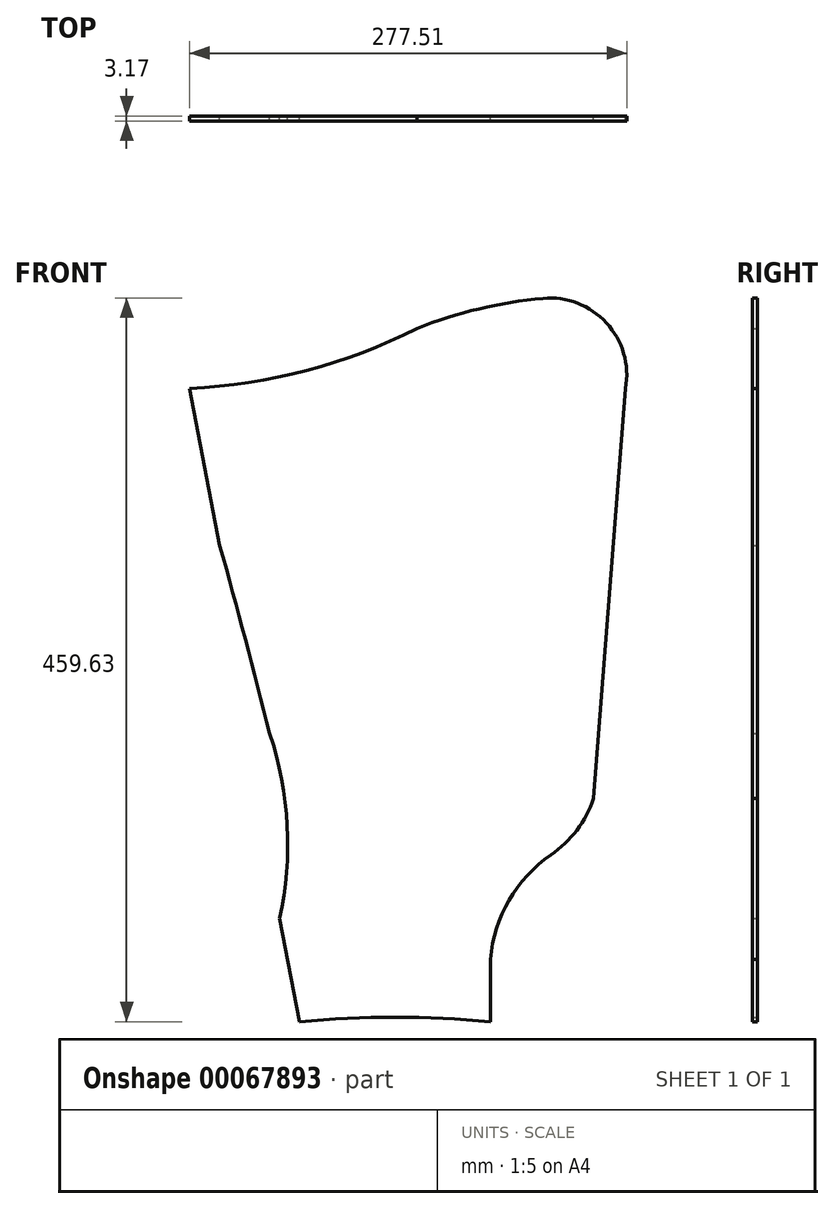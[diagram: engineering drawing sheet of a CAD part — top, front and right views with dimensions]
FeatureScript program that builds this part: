
annotation { "Feature Type Name" : "Feature", "Feature Type Description" : "" }
export const myFeature = defineFeature(function(context is Context, id is Id, definition is map)
    precondition{}
    {
        {
            var Q0;
            Q0=qCreatedBy(makeId("Front.planeOp"),FACE);
            var sketch = newSketch(context, id + "F0", { "sketchPlane" : qUnion([Q0])});
            skArc(sketch, "E0", {"start": v(121.1, 0) * mm, "mid": v(60.55, 2.84) * mm, "end": v(0, 0) * mm});
            skLineSegment(sketch, "E1", {"start": v(0, 0) * mm, "end": v(-12.7, 65.45) * mm});
            skArc(sketch, "E2", {"start": v(-12.7, 65.45) * mm, "mid": v(-7.96, 124.62) * mm, "end": v(-19.05, 182.93) * mm});
            skLineSegment(sketch, "E3", {"start": v(-50.8, 302.48) * mm, "end": v(-69.85, 402.28) * mm});
            skArc(sketch, "E4", {"start": v(-69.85, 402.28) * mm, "mid": v(4.31, 413.68) * mm, "end": v(74.43, 440.38) * mm});
            skArc(sketch, "E5", {"start": v(206.9, 402.28) * mm, "mid": v(194.82, 443.84) * mm, "end": v(154.45, 459.43) * mm});
            skLineSegment(sketch, "E6", {"start": v(206.9, 402.28) * mm, "end": v(186.7, 141.68) * mm});
            skArc(sketch, "E7", {"start": v(159.53, 105.9) * mm, "mid": v(175.98, 121.61) * mm, "end": v(186.7, 141.68) * mm});
            skArc(sketch, "E8", {"start": v(154.45, 459.43) * mm, "mid": v(113.76, 452.76) * mm, "end": v(74.43, 440.38) * mm});
            skArc(sketch, "E9", {"start": v(-19.05, 182.93) * mm, "mid": v(-34.53, 242.8) * mm, "end": v(-50.8, 302.48) * mm});
            skArc(sketch, "E10", {"start": v(159.53, 105.9) * mm, "mid": v(132.9, 77.1) * mm, "end": v(121.1, 39.7) * mm});
            skLineSegment(sketch, "E11", {"start": v(121.1, 39.7) * mm, "end": v(121.1, 0) * mm});
            skSolve(sketch);
        }
        {
            var Q0;
            Q0=makeQuery(id+"F0.imprint","IMPRINT",FACE,{"disambiguationData":[TD([[makeQuery(id+"F0.imprint","IMPRINT",EDGE,{"derivedFrom":sQuery(id+"F0.wireOp",EDGE,"E0")}),-1.0]])]});
            extrude(context, id + "F1", {"entities" : qUnion([Q0]), "depth" : 3.17 * mm});
        }
    });
